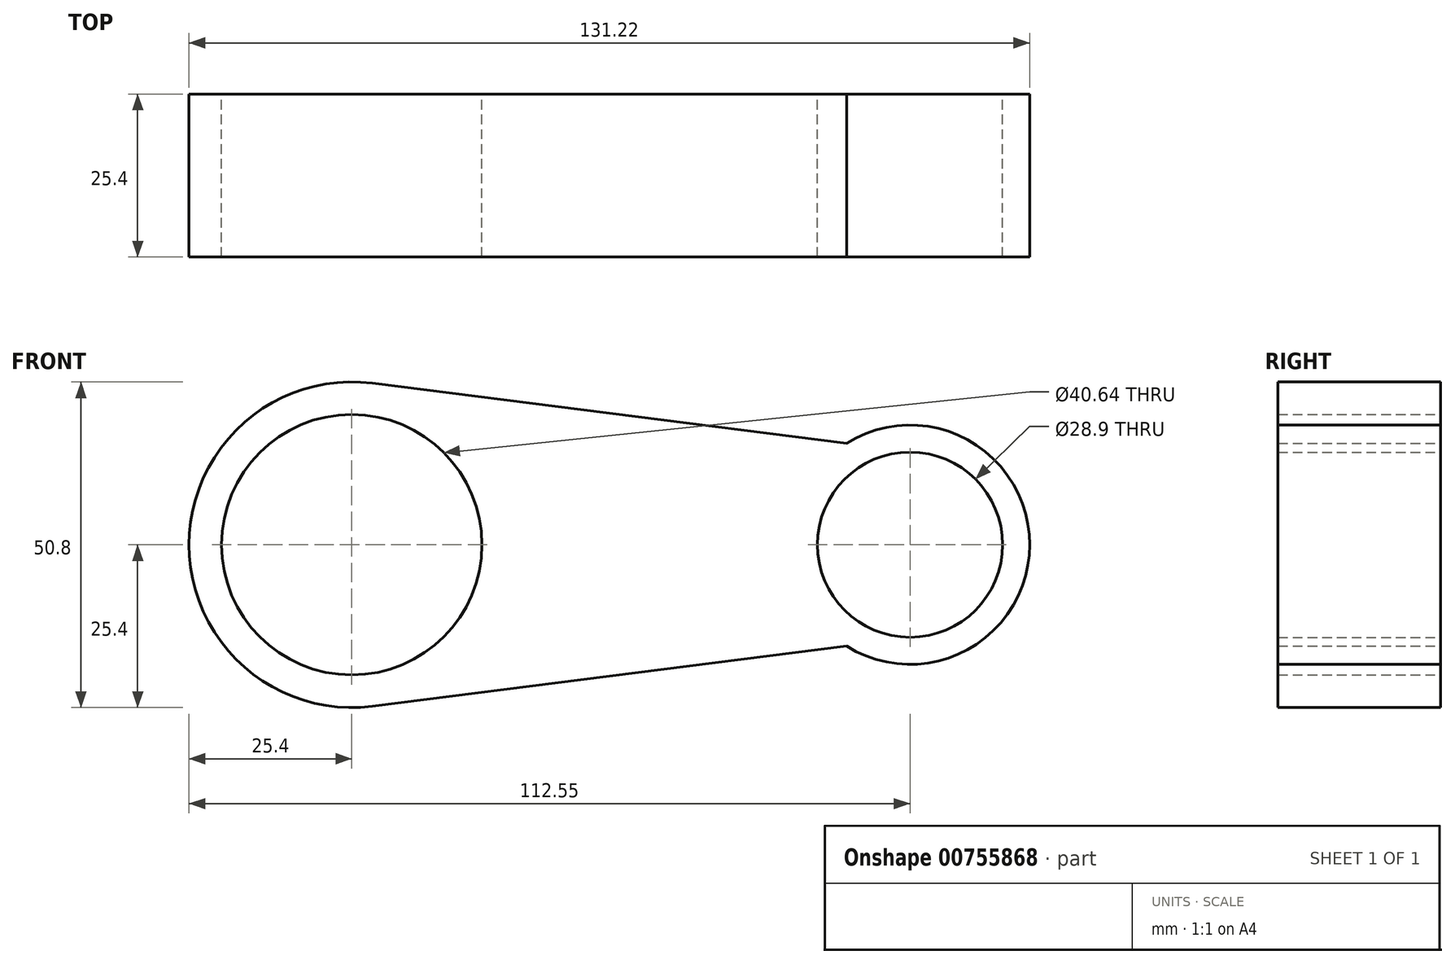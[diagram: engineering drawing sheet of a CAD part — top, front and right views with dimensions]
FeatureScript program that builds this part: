
annotation { "Feature Type Name" : "Feature", "Feature Type Description" : "" }
export const myFeature = defineFeature(function(context is Context, id is Id, definition is map)
    precondition{}
    {
        {
            var Q0;
            Q0=qCreatedBy(makeId("Front.planeOp"),FACE);
            var sketch = newSketch(context, id + "F0", { "sketchPlane" : qUnion([Q0])});
            skCircle(sketch, "E0", {"center": v(0, 0) * mm, "radius": 25.4 * mm});
            skCircle(sketch, "E1", {"center": v(87.15, 0) * mm, "radius": 14.45 * mm});
            skLineSegment(sketch, "E2", {"start": v(3.2, 25.2) * mm, "end": v(88.97, 14.34) * mm});
            skLineSegment(sketch, "E3", {"start": v(3.2, -25.2) * mm, "end": v(88.97, -14.34) * mm});
            skCircle(sketch, "E4", {"center": v(0, 0) * mm, "radius": 20.32 * mm});
            skCircle(sketch, "E5", {"center": v(87.15, 0) * mm, "radius": 18.67 * mm});
            skSolve(sketch);
        }
        {
            var Q0;
            Q0 = qSketchRegion(id + "F0", true);
            extrude(context, id + "F1", {"entities" : qUnion([Q0]), "depth" : 25.4 * mm, "offsetDistance" : 25.4 * mm});
        }
    });
